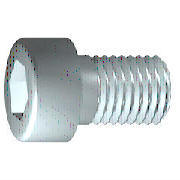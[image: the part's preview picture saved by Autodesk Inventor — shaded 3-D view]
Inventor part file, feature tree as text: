
AUTODESK INVENTOR PART (.ipt)
format: ipt  version: 2022 (Build 260153000, 153)  size: 186,368 bytes
history: native  units: mm (DEFAULTED — no unit token found)
features: sketch x2, extrude x1, plane x1, fillet x1
ambient origin geometry x7: Origin, YZ Plane, XY Plane, X Axis, Y Axis, Z Axis, Center Point
bodies: Solid1 (feature_tree), Body (feature_tree)
feature tree (5):
  extrude  "Slot"  Depth=6.0mm
  plane  "Work Plane1"
  fillet  "Fillet2"  Radius=6.0mm
  sketch  "Sketch1"  dims[d1=24.0mm d2=0.61355mm d3=6.0mm]
  sketch  "Sketch2"  dims[d4=3.0mm d5=60.0deg d6=6.0mm d7=6.0mm d8=5.773503mm d9=10.0mm d10=90.0deg d11=10.0mm d12=0.0mm d13=24.0mm d14=0.0mm d15=0.61345mm d16=0.61345mm d17=0.6mm d19=0.0mm d26=55.0mm d27=45.0deg d28=0.0mm d29=0.0mm d30=0.1mm]
